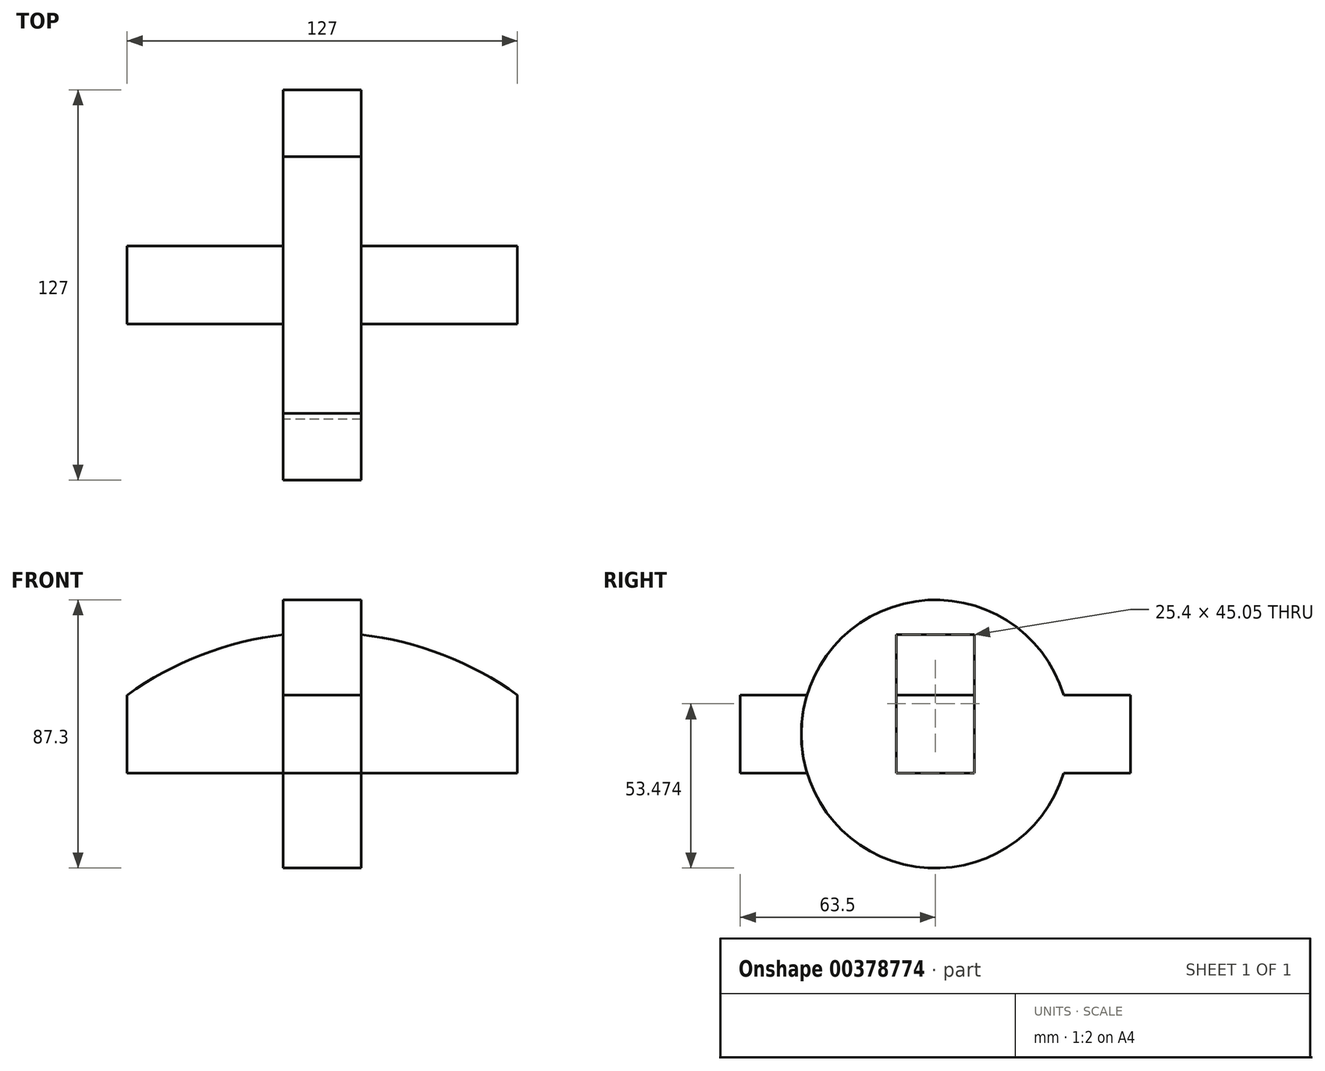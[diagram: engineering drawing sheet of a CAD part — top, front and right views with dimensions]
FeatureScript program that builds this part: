
annotation { "Feature Type Name" : "Feature", "Feature Type Description" : "" }
export const myFeature = defineFeature(function(context is Context, id is Id, definition is map)
    precondition{}
    {
        {
            var Q0;
            Q0=qCreatedBy(makeId("Front.planeOp"),FACE);
            var sketch = newSketch(context, id + "F0", { "sketchPlane" : qUnion([Q0])});
            skLineSegment(sketch, "E0.bottom", {"start": v(-63.5, 12.7) * mm, "end": v(63.5, 12.7) * mm});
            skLineSegment(sketch, "E0.top", {"start": v(-63.5, -12.7) * mm, "end": v(63.5, -12.7) * mm});
            skLineSegment(sketch, "E0.left", {"start": v(-63.5, 12.7) * mm, "end": v(-63.5, -12.7) * mm});
            skLineSegment(sketch, "E0.right", {"start": v(63.5, 12.7) * mm, "end": v(63.5, -12.7) * mm});
            skPoint(sketch, "E0.middle", {"position": v(0, 0) * mm});
            skArc(sketch, "E1", {"start": v(63.5, 12.7) * mm, "mid": v(0, 33.09) * mm, "end": v(-63.5, 12.7) * mm});
            skSolve(sketch);
        }
        {
            var Q0;
            Q0=qCreatedBy(makeId("Right.planeOp"),FACE);
            var sketch = newSketch(context, id + "F1", { "sketchPlane" : qUnion([Q0])});
            skLineSegment(sketch, "E2.bottom", {"start": v(-63.5, 12.7) * mm, "end": v(63.5, 12.7) * mm});
            skLineSegment(sketch, "E2.top", {"start": v(-63.5, -12.7) * mm, "end": v(63.5, -12.7) * mm});
            skLineSegment(sketch, "E2.left", {"start": v(-63.5, 12.7) * mm, "end": v(-63.5, -12.7) * mm});
            skLineSegment(sketch, "E2.right", {"start": v(63.5, 12.7) * mm, "end": v(63.5, -12.7) * mm});
            skPoint(sketch, "E2.middle", {"position": v(0, 0) * mm});
            skCircle(sketch, "E3", {"center": v(0, 0) * mm, "radius": 43.65 * mm});
            skSolve(sketch);
        }
        {
            var Q0;
            Q0=makeQuery(id+"F0.imprint","IMPRINT",FACE,{"disambiguationData":[TD([[makeQuery(id+"F0.imprint","IMPRINT",EDGE,{"derivedFrom":sQuery(id+"F0.wireOp",EDGE,"E0.bottom")}),-1.0]])]});
            extrude(context, id + "F2", {"entities" : qUnion([Q0]), "endBound" : BoundingType.SYMMETRIC, "depth" : 25.4 * mm});
        }
        {
            var Q0;
            {var subQ0=sQuery(id+"F1.wireOp",EDGE,"E2.left");Q0=makeQuery(id+"F1.imprint","IMPRINT",FACE,{"disambiguationData":[TD([[makeQuery(id+"F1.imprint","IMPRINT",EDGE,{"derivedFrom":subQ0}),1.0]])]});}
            extrude(context, id + "F3", {"entities" : qUnion([Q0]), "endBound" : BoundingType.SYMMETRIC, "depth" : 25.4 * mm});
        }
        {
            var Q0;
            Q0=makeQuery(id+"F0.imprint","IMPRINT",FACE,{"disambiguationData":[TD([[makeQuery(id+"F0.imprint","IMPRINT",EDGE,{"derivedFrom":sQuery(id+"F0.wireOp",EDGE,"E0.bottom")}),1.0]])]});
            extrude(context, id + "F4", {"entities" : qUnion([Q0]), "operationType" : NewBodyOperationType.ADD, "endBound" : BoundingType.SYMMETRIC, "depth" : 25.4 * mm});
        }
        {
            var Q0;
            {var subQ0=sQuery(id+"F1.wireOp",EDGE,"E3");var subQ1=sQuery(id+"F1.wireOp",EDGE,"E2.bottom");var subQ2=makeQuery(id+"F1.imprint","INTERSECT",VERTEX,{"disambiguationData":[OD(0.0)],"derivedFrom":[subQ1,subQ0]});Q0=makeQuery(id+"F1.imprint","IMPRINT",FACE,{"disambiguationData":[TD([[makeQuery(id+"F1.imprint","IMPRINT",EDGE,{"disambiguationData":[TD([[subQ2,-1.0]])],"derivedFrom":subQ1}),1.0]])]});}
            extrude(context, id + "F5", {"entities" : qUnion([Q0]), "operationType" : NewBodyOperationType.ADD, "endBound" : BoundingType.SYMMETRIC, "depth" : 25.4 * mm});
        }
        {
            var Q0;
            {var subQ0=sQuery(id+"F1.wireOp",EDGE,"E3");var subQ1=sQuery(id+"F1.wireOp",EDGE,"E2.bottom");var subQ2=makeQuery(id+"F1.imprint","INTERSECT",VERTEX,{"disambiguationData":[OD(0.0)],"derivedFrom":[subQ1,subQ0]});Q0=makeQuery(id+"F1.imprint","IMPRINT",FACE,{"disambiguationData":[TD([[makeQuery(id+"F1.imprint","IMPRINT",EDGE,{"disambiguationData":[TD([[subQ2,-1.0]])],"derivedFrom":subQ1}),-1.0]])]});}
            extrude(context, id + "F6", {"entities" : qUnion([Q0]), "endBound" : BoundingType.SYMMETRIC, "depth" : 25.4 * mm});
        }
        {
            var Q0;
            {var subQ0=sQuery(id+"F1.wireOp",EDGE,"E3");var subQ1=sQuery(id+"F1.wireOp",EDGE,"E2.top");var subQ2=makeQuery(id+"F1.imprint","INTERSECT",VERTEX,{"disambiguationData":[OD(0.0)],"derivedFrom":[subQ1,subQ0]});Q0=makeQuery(id+"F1.imprint","IMPRINT",FACE,{"disambiguationData":[TD([[makeQuery(id+"F1.imprint","IMPRINT",EDGE,{"disambiguationData":[TD([[subQ2,-1.0]])],"derivedFrom":subQ1}),-1.0]])]});}
            extrude(context, id + "F7", {"entities" : qUnion([Q0]), "endBound" : BoundingType.SYMMETRIC, "depth" : 25.4 * mm});
        }
        {
            var Q0;
            {var subQ0=sQuery(id+"F1.wireOp",EDGE,"E2.right");Q0=makeQuery(id+"F1.imprint","IMPRINT",FACE,{"disambiguationData":[TD([[makeQuery(id+"F1.imprint","IMPRINT",EDGE,{"derivedFrom":subQ0}),-1.0]])]});}
            extrude(context, id + "F8", {"entities" : qUnion([Q0]), "operationType" : NewBodyOperationType.ADD, "endBound" : BoundingType.SYMMETRIC, "depth" : 25.4 * mm});
        }
    });
